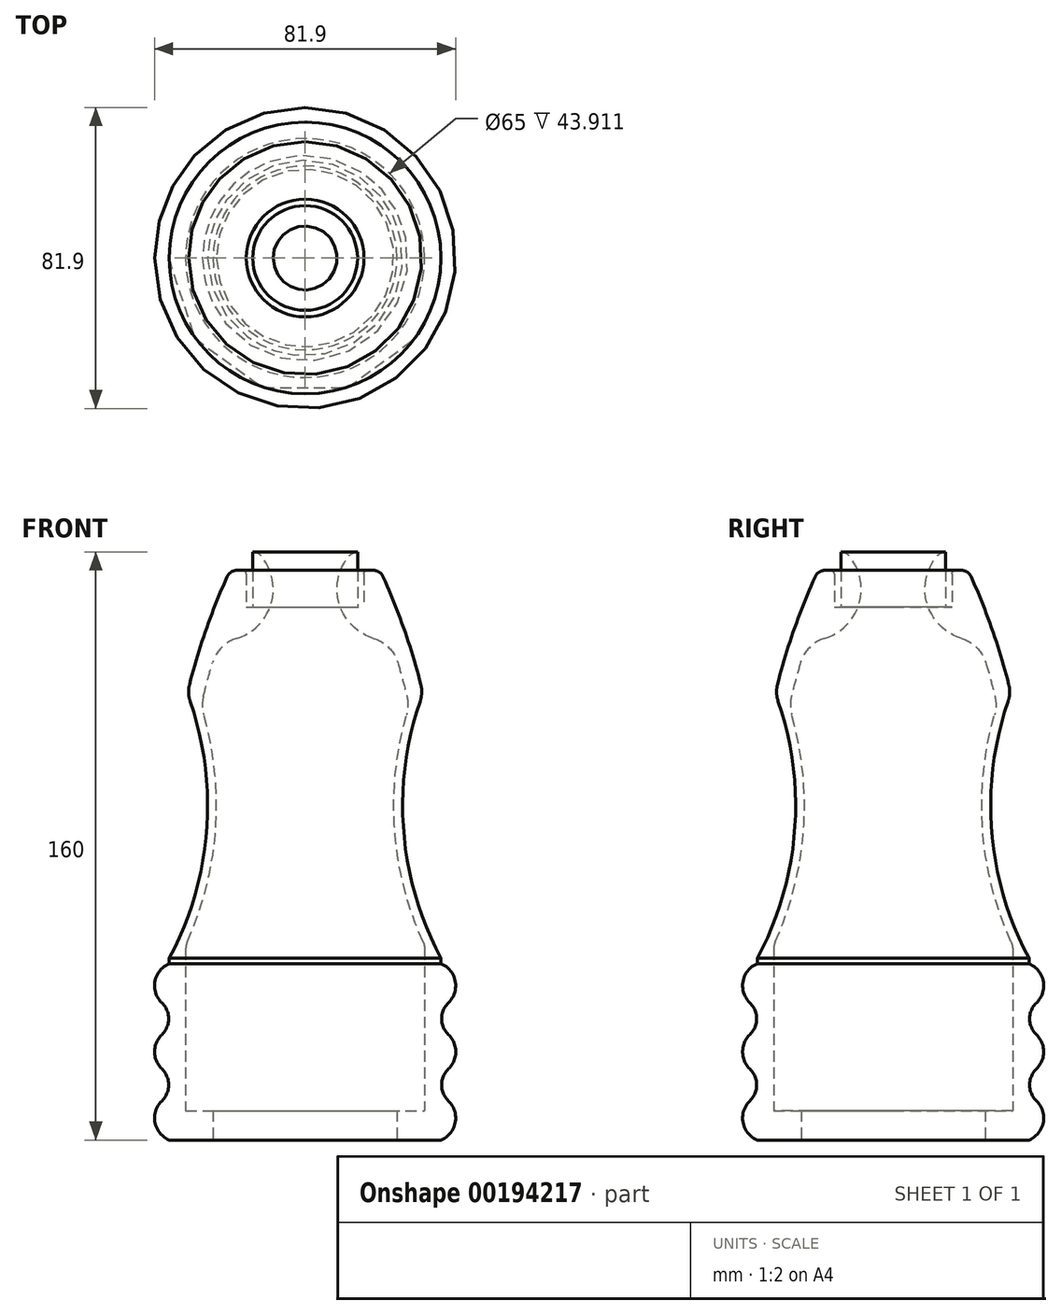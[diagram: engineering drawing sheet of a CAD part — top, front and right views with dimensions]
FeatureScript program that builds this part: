
annotation { "Feature Type Name" : "Feature", "Feature Type Description" : "" }
export const myFeature = defineFeature(function(context is Context, id is Id, definition is map)
    precondition{}
    {
        {
            var Q0;
            Q0=qCreatedBy(makeId("Front.planeOp"),FACE);
            var sketch = newSketch(context, id + "F0", { "sketchPlane" : qUnion([Q0])});
            skLineSegment(sketch, "E0", {"start": v(25, 0) * mm, "end": v(36.95, 0) * mm});
            skLineSegment(sketch, "E1", {"start": v(25, 0) * mm, "end": v(25, 8) * mm});
            skLineSegment(sketch, "E2", {"start": v(25, 8) * mm, "end": v(32.5, 8) * mm});
            skLineSegment(sketch, "E3", {"start": v(32.5, 8) * mm, "end": v(32.5, 51.91) * mm});
            skLineSegment(sketch, "E4", {"start": v(14.25, 160) * mm, "end": v(14.3, 160) * mm});
            skLineSegment(sketch, "E5", {"start": v(36.95, 0) * mm, "end": v(36.95, 80) * mm});
            skArc(sketch, "E6", {"start": v(31.46, 123.93) * mm, "mid": v(26.98, 138.8) * mm, "end": v(21.22, 153.23) * mm});
            skArc(sketch, "E7", {"start": v(27.68, 120.67) * mm, "mid": v(26.5, 125.26) * mm, "end": v(25.2, 129.82) * mm});
            skArc(sketch, "E8", {"start": v(12, 158.94) * mm, "mid": v(9.25, 145.96) * mm, "end": v(18.57, 136.5) * mm});
            skArc(sketch, "E9", {"start": v(27.57, 115.59) * mm, "mid": v(24.36, 84.38) * mm, "end": v(32.06, 53.96) * mm});
            skArc(sketch, "E10", {"start": v(36.95, 0) * mm, "mid": v(40.95, 6) * mm, "end": v(36.95, 12) * mm});
            skArc(sketch, "E11", {"start": v(36.95, 18) * mm, "mid": v(40.95, 24) * mm, "end": v(36.95, 30) * mm});
            skArc(sketch, "E12", {"start": v(36.95, 36) * mm, "mid": v(40.95, 42) * mm, "end": v(36.95, 48) * mm});
            skLineSegment(sketch, "E13", {"start": v(34.45, 6) * mm, "end": v(34.45, 42) * mm, "construction": true});
            skPoint(sketch, "E14.visualSharp", {"position": v(18, 160) * mm});
            skPoint(sketch, "E15.visualSharp", {"position": v(13, 160) * mm});
            skArc(sketch, "E15.filletArc", {"start": v(14.3, 160) * mm, "mid": v(13.03, 159.72) * mm, "end": v(12, 158.94) * mm});
            skArc(sketch, "E16.trimOffspring", {"start": v(13.12, 159.76) * mm, "mid": v(13.06, 159.88) * mm, "end": v(13, 160) * mm, "construction": true});
            skPoint(sketch, "E17.visualSharp", {"position": v(28.3, 118) * mm});
            skArc(sketch, "E17.filletArc", {"start": v(27.57, 115.59) * mm, "mid": v(27.95, 118.12) * mm, "end": v(27.68, 120.67) * mm});
            skPoint(sketch, "E18.visualSharp", {"position": v(23.27, 135.9) * mm});
            skArc(sketch, "E18.filletArc", {"start": v(25.2, 129.82) * mm, "mid": v(22.73, 134) * mm, "end": v(18.57, 136.5) * mm});
            skPoint(sketch, "E19.visualSharp", {"position": v(32.5, 53) * mm});
            skArc(sketch, "E19.filletArc", {"start": v(32.5, 51.91) * mm, "mid": v(32.39, 52.96) * mm, "end": v(32.06, 53.96) * mm});
            skArc(sketch, "E20", {"start": v(38.96, 37.32) * mm, "mid": v(37.13, 33) * mm, "end": v(38.96, 28.68) * mm});
            skArc(sketch, "E21", {"start": v(38.96, 19.32) * mm, "mid": v(37.13, 15) * mm, "end": v(38.96, 10.68) * mm});
            skLineSegment(sketch, "E22", {"start": v(0, 0) * mm, "end": v(0, 180.5) * mm, "construction": true});
            skLineSegment(sketch, "E23.top", {"start": v(14.25, 145) * mm, "end": v(16, 145) * mm});
            skLineSegment(sketch, "E23.left", {"start": v(14.25, 160) * mm, "end": v(14.25, 145) * mm});
            skLineSegment(sketch, "E23.right", {"start": v(16, 154) * mm, "end": v(16, 145) * mm});
            skLineSegment(sketch, "E24.trimOffspring", {"start": v(16, 160) * mm, "end": v(16.14, 160) * mm});
            skArc(sketch, "E25.0", {"start": v(31.27, 119.36) * mm, "mid": v(26.81, 83.82) * mm, "end": v(36.95, 49.46) * mm});
            skPoint(sketch, "E26.visualSharp", {"position": v(32.05, 121.53) * mm});
            skArc(sketch, "E26.filletArc", {"start": v(31.27, 119.36) * mm, "mid": v(31.7, 121.63) * mm, "end": v(31.46, 123.93) * mm});
            skLineSegment(sketch, "E27", {"start": v(17, 155) * mm, "end": v(18.49, 155) * mm});
            skArc(sketch, "E28.filletArc", {"start": v(21.22, 153.23) * mm, "mid": v(20.11, 154.52) * mm, "end": v(18.49, 155) * mm});
            skArc(sketch, "E29.filletArc", {"start": v(17, 155) * mm, "mid": v(16.3, 154.7) * mm, "end": v(16, 154) * mm});
            skSolve(sketch);
        }
        {
            var Q0;
            {var subQ4=sQuery(id+"F0.wireOp",EDGE,"E0");Q0=makeQuery(id+"F0.imprint","IMPRINT",FACE,{"disambiguationData":[TD([[makeQuery(id+"F0.imprint","IMPRINT",EDGE,{"derivedFrom":subQ4}),1.0]])]});}
            var Q1;
            {var subQ0=sQuery(id+"F0.wireOp",EDGE,"E10");var subQ1=sQuery(id+"F0.wireOp",EDGE,"E5");var subQ3=makeQuery(id+"F0.imprint","INTERSECT",VERTEX,{"derivedFrom":[subQ1,subQ0]});Q1=makeQuery(id+"F0.imprint","IMPRINT",FACE,{"disambiguationData":[TD([[makeQuery(id+"F0.imprint","IMPRINT",EDGE,{"disambiguationData":[TD([[subQ3,1.0]])],"derivedFrom":subQ0}),1.0]])]});}
            var Q2;
            {var subQ5=sQuery(id+"F0.wireOp",EDGE,"E21");Q2=makeQuery(id+"F0.imprint","IMPRINT",FACE,{"disambiguationData":[TD([[makeQuery(id+"F0.imprint","IMPRINT",EDGE,{"derivedFrom":subQ5}),-1.0]])]});}
            var Q3;
            {var subQ0=sQuery(id+"F0.wireOp",EDGE,"E11");var subQ1=sQuery(id+"F0.wireOp",EDGE,"E5");var subQ2=makeQuery(id+"F0.imprint","INTERSECT",VERTEX,{"disambiguationData":[OD(0.0)],"derivedFrom":[subQ1,subQ0]});Q3=makeQuery(id+"F0.imprint","IMPRINT",FACE,{"disambiguationData":[TD([[makeQuery(id+"F0.imprint","IMPRINT",EDGE,{"disambiguationData":[TD([[subQ2,-1.0]])],"derivedFrom":subQ1}),-1.0]])]});}
            var Q4;
            {var subQ5=sQuery(id+"F0.wireOp",EDGE,"E20");Q4=makeQuery(id+"F0.imprint","IMPRINT",FACE,{"disambiguationData":[TD([[makeQuery(id+"F0.imprint","IMPRINT",EDGE,{"derivedFrom":subQ5}),-1.0]])]});}
            var Q5;
            {var subQ0=sQuery(id+"F0.wireOp",EDGE,"E12");var subQ1=sQuery(id+"F0.wireOp",EDGE,"E5");var subQ2=makeQuery(id+"F0.imprint","INTERSECT",VERTEX,{"disambiguationData":[OD(0.0)],"derivedFrom":[subQ1,subQ0]});Q5=makeQuery(id+"F0.imprint","IMPRINT",FACE,{"disambiguationData":[TD([[makeQuery(id+"F0.imprint","IMPRINT",EDGE,{"disambiguationData":[TD([[subQ2,-1.0]])],"derivedFrom":subQ1}),-1.0]])]});}
            var Q6;
            {var subQ3=sQuery(id+"F0.wireOp",EDGE,"FOnpjjQI-xOYA-vLoJ-Nxkc-kSVceBM1n9f2");Q6=makeQuery(id+"F0.imprint","IMPRINT",FACE,{"disambiguationData":[TD([[makeQuery(id+"F0.imprint","IMPRINT",EDGE,{"derivedFrom":subQ3}),-1.0]])]});}
            var Q7;
            Q7=sQuery(id+"F0.wireOp",EDGE,"E22");
            revolve(context, id + "F1", {"entities" : qUnion([Q0, Q1, Q2, Q3, Q4, Q5, Q6]), "axis" : qUnion([Q7]), "revolveType" : RevolveType.FULL});
        }
    });
